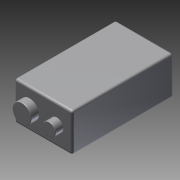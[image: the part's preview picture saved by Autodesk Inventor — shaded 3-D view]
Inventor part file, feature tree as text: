
AUTODESK INVENTOR PART (.ipt)
format: ipt  version: 2013 (Build 170138000, 138)  size: 118,784 bytes
history: native  units: in
note: dims shown in document units (in); Inventor stores cm internally (conversion verified against a paired STEP export)
features: extrude x2, fillet x2, sketch x2, plane x1
ambient origin geometry x8: Origin, YZ Plane, XZ Plane, XY Plane, X Axis, Y Axis, Z Axis, Center Point
bodies: Solid1 (feature_tree)
feature tree (7):
  extrude  "Extrusion1"  Depth=0.689in
  fillet  "Fillet1"  Radius=1.827in
  extrude  "Extrusion2"  Depth=0.142in TaperAngle=0.0deg
  fillet  "Fillet2"  Radius=0.01in
  plane  "Work Plane1"
  sketch  "Sketch1"  dims[d0=1.043in d1=0.689in d2=1.827in d3=0.0in]
  sketch  "Sketch2"  dims[d4=0.039in d5=0.142in d6=0.0in d7=0.01in]
